# Revit family: Electronics_BYOM-Room-Solution_Biamp_MAX-Connect
name_source: partatom
category: Communication Devices
units: mm (PartAtom-declared; Revit-internal decimal feet)

## family parameters
Cut with Voids When Loaded = No
Host = Face
Maintain Annotation Orientation = No
OmniClass Number = 23.85.10.14.21
OmniClass Title = Presentation Systems
Part Type = Normal
Room Calculation Point = No
Round Connector Dimension = Use Diameter
Shared = No

## types (1)
- MAX Connect
    Apparent Load = 7 VA
    Connector Description = Power connector, 12V, 2A DC
    Default Elevation = 1219 mm
    Depth = 127 mm  [stored 0.416667 ft]
    Description = MAX Connect BYOM Room Solution
    Frequency Band = 2.4Ghz
    Height = 25 mm
    Housing Material = Biamp - Metal - Black
    Humidity = 10%–90 %
    Manufacturer = Biamp
    Max Power Consumption = 7 W
    Maximum Transmit Power = 2.45dBm
    Model = MAX Connect
    Noise Level = 40–43dB(Background noise< 18db, 1M,mute room)
    Number of Poles = 1
    Power Factor = 1
    Product Documentation Link = https://use1-admin.rhyl.inforcloudsuite.com
    Product Page URL = https://products.biamp.com
    Product data url = https://bimobject.com
    Temperature Range = 68-140F (20-60C)
    URL = https://www.biamp.com
    Version = 1
    Voltage = 12 V
    Weight = 1.20 lbf
    Width = 127 mm  [stored 0.416667 ft]
    Wireless Range = Up to 30ft (10 m)

note: [stored X ft] marks values corroborated as IEEE doubles in the binary element streams (Revit-internal decimal feet)

## geometry (parser evidence)
native form markers: Sweep x3
no freeform markers — native parametric forms only
